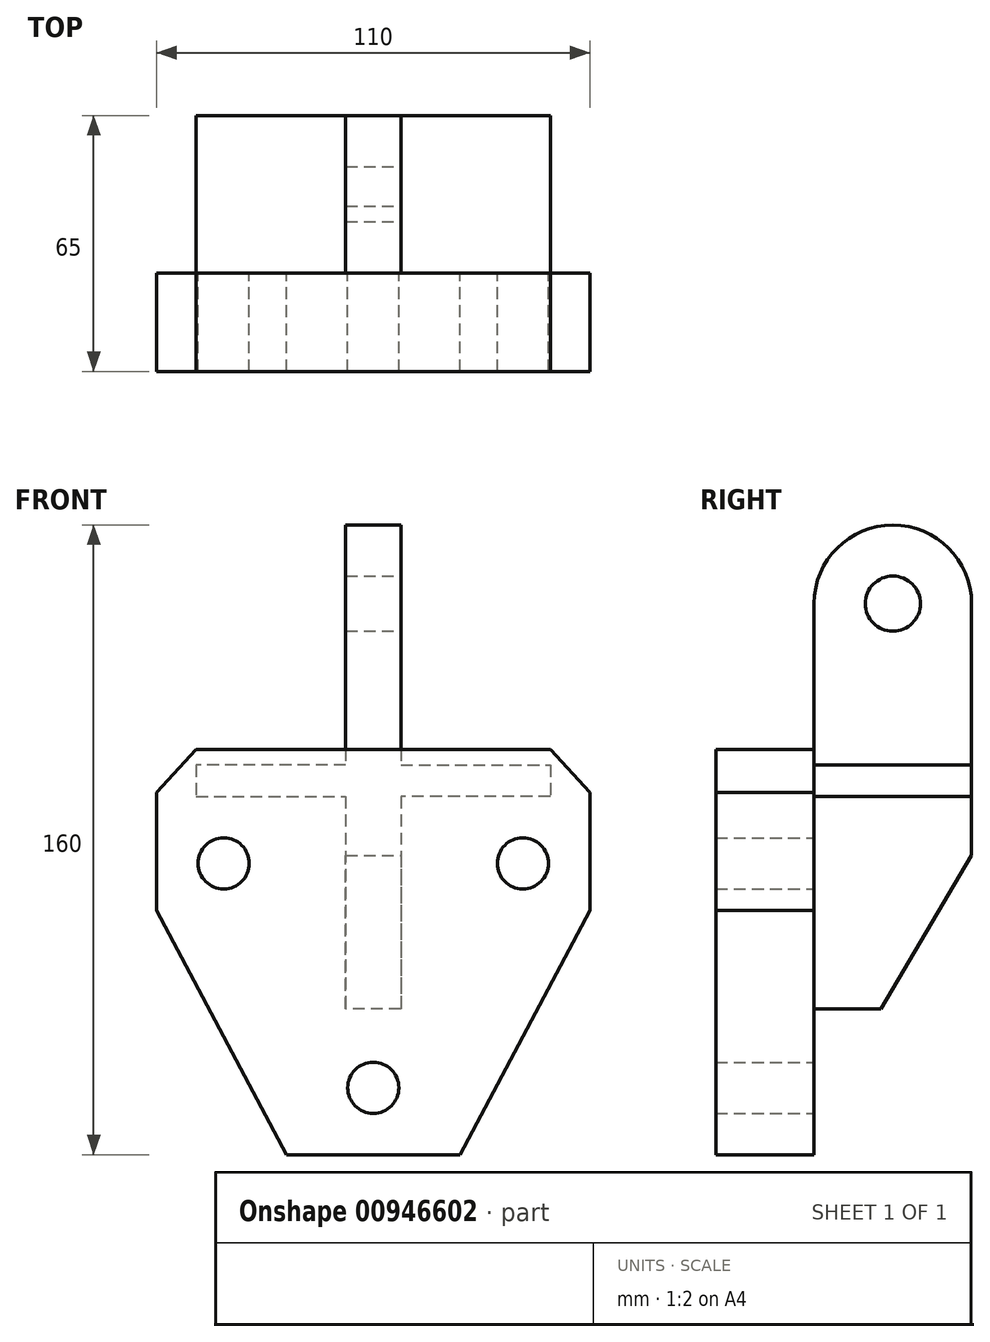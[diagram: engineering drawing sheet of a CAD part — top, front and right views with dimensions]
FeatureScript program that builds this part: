
annotation { "Feature Type Name" : "Feature", "Feature Type Description" : "" }
export const myFeature = defineFeature(function(context is Context, id is Id, definition is map)
    precondition{}
    {
        {
            var Q0;
            Q0=qCreatedBy(makeId("Front.planeOp"),FACE);
            var sketch = newSketch(context, id + "F0", { "sketchPlane" : qUnion([Q0])});
            skLineSegment(sketch, "E0", {"start": v(0, 51.49) * mm, "end": v(-45, 51.49) * mm});
            skLineSegment(sketch, "E1", {"start": v(-45, 51.49) * mm, "end": v(-55, 40.49) * mm});
            skLineSegment(sketch, "E2", {"start": v(-55, 40.49) * mm, "end": v(-55, 10.49) * mm});
            skLineSegment(sketch, "E3", {"start": v(-55, 10.49) * mm, "end": v(-22, -51.51) * mm});
            skLineSegment(sketch, "E4", {"start": v(-22, -51.51) * mm, "end": v(0, -51.51) * mm});
            skLineSegment(sketch, "E5", {"start": v(0, -51.51) * mm, "end": v(0, 51.49) * mm});
            skCircle(sketch, "E6", {"center": v(-38, 22.49) * mm, "radius": 6.5 * mm});
            skArc(sketch, "E7", {"start": v(0, -28.01) * mm, "mid": v(-6.5, -34.51) * mm, "end": v(0, -41.01) * mm});
            skLineSegment(sketch, "E8.MirrorCS", {"start": v(0, 51.49) * mm, "end": v(45, 51.49) * mm});
            skLineSegment(sketch, "E9.MirrorCS", {"start": v(45, 51.49) * mm, "end": v(55, 40.49) * mm});
            skLineSegment(sketch, "E10.MirrorCS", {"start": v(55, 40.49) * mm, "end": v(55, 10.49) * mm});
            skLineSegment(sketch, "E11.MirrorCS", {"start": v(55, 10.49) * mm, "end": v(22, -51.51) * mm});
            skLineSegment(sketch, "E12.MirrorCS", {"start": v(22, -51.51) * mm, "end": v(0, -51.51) * mm});
            skArc(sketch, "E13.MirrorCS", {"start": v(0, -28.01) * mm, "mid": v(6.5, -34.51) * mm, "end": v(0, -41.01) * mm});
            skCircle(sketch, "E14.MirrorC", {"center": v(38, 22.49) * mm, "radius": 6.5 * mm});
            skSolve(sketch);
        }
        {
            var Q0;
            Q0 = qSketchRegion(id + "F0", true);
            extrude(context, id + "F1", {"entities" : qUnion([Q0]), "depth" : 25 * mm, "offsetDistance" : 25 * mm});
        }
        {
            var Q0;
            Q0=makeQuery(id+"F1.opExtrude","CAP_FACE",FACE,{"disambiguationData":[OSD([sQuery(id+"F0.wireOp",EDGE,"E0"),sQuery(id+"F0.wireOp",EDGE,"E1"),sQuery(id+"F0.wireOp",EDGE,"E2"),sQuery(id+"F0.wireOp",EDGE,"E3"),sQuery(id+"F0.wireOp",EDGE,"E4"),sQuery(id+"F0.wireOp",EDGE,"E6"),sQuery(id+"F0.wireOp",EDGE,"E7"),sQuery(id+"F0.wireOp",EDGE,"E8.MirrorCS"),sQuery(id+"F0.wireOp",EDGE,"E9.MirrorCS"),sQuery(id+"F0.wireOp",EDGE,"E10.MirrorCS"),sQuery(id+"F0.wireOp",EDGE,"E11.MirrorCS"),sQuery(id+"F0.wireOp",EDGE,"E12.MirrorCS"),sQuery(id+"F0.wireOp",EDGE,"E13.MirrorCS"),sQuery(id+"F0.wireOp",EDGE,"E14.MirrorC")])],"isStart":true});
            var sketch = newSketch(context, id + "F2", { "sketchPlane" : qUnion([Q0])});
            skLineSegment(sketch, "E15", {"start": v(0, 108.49) * mm, "end": v(-7, 108.49) * mm});
            skLineSegment(sketch, "E16", {"start": v(-7, 108.49) * mm, "end": v(-7, 47.49) * mm});
            skLineSegment(sketch, "E17", {"start": v(-7, 47.49) * mm, "end": v(-45, 47.49) * mm});
            skLineSegment(sketch, "E18", {"start": v(-45, 47.49) * mm, "end": v(-45, 39.49) * mm});
            skLineSegment(sketch, "E19", {"start": v(-45, 39.49) * mm, "end": v(-7, 39.49) * mm});
            skLineSegment(sketch, "E20", {"start": v(-7, 39.49) * mm, "end": v(-7, -14.51) * mm});
            skLineSegment(sketch, "E21", {"start": v(-7, -14.51) * mm, "end": v(0, -14.51) * mm});
            skLineSegment(sketch, "E22.MirrorCS", {"start": v(0, 108.49) * mm, "end": v(7, 108.49) * mm});
            skLineSegment(sketch, "E23.MirrorCS", {"start": v(7, 108.49) * mm, "end": v(7, 47.49) * mm});
            skLineSegment(sketch, "E24.MirrorCS", {"start": v(7, 47.49) * mm, "end": v(45, 47.49) * mm});
            skLineSegment(sketch, "E25.MirrorCS", {"start": v(45, 47.49) * mm, "end": v(45, 39.49) * mm});
            skLineSegment(sketch, "E26.MirrorCS", {"start": v(45, 39.49) * mm, "end": v(7, 39.49) * mm});
            skLineSegment(sketch, "E27.MirrorCS", {"start": v(7, 39.49) * mm, "end": v(7, -14.51) * mm});
            skLineSegment(sketch, "E28.MirrorCS", {"start": v(7, -14.51) * mm, "end": v(0, -14.51) * mm});
            skSolve(sketch);
        }
        {
            var Q0;
            Q0 = qSketchRegion(id + "F2", true);
            extrude(context, id + "F3", {"entities" : qUnion([Q0]), "operationType" : NewBodyOperationType.ADD, "depth" : 40 * mm, "offsetDistance" : 25 * mm});
        }
        {
            var Q0;
            Q0=makeQuery(id+"F3.opExtrude","CAP_EDGE",EDGE,{"disambiguationData":[OSD([sQuery(id+"F2.wireOp",EDGE,"E15"),sQuery(id+"F2.wireOp",EDGE,"E22.MirrorCS")])],"isStart":true});
            var Q1;
            Q1=makeQuery(id+"F3.opExtrude","CAP_EDGE",EDGE,{"disambiguationData":[OSD([sQuery(id+"F2.wireOp",EDGE,"E15"),sQuery(id+"F2.wireOp",EDGE,"E22.MirrorCS")])],"isStart":false});
            fillet(context, id + "F4", {"entities" : qUnion([Q0, Q1]), "radius" : 20 * mm, "tangentPropagation" : true, "allowEdgeOverflow" : false});
        }
        {
            var Q0;
            Q0=makeQuery(id+"F3.opExtrude","SWEPT_FACE",FACE,{"disambiguationData":[OSD([sQuery(id+"F2.wireOp",EDGE,"E16")])]});
            var sketch = newSketch(context, id + "F5", { "sketchPlane" : qUnion([Q0])});
            skCircle(sketch, "E29", {"center": v(20, 88.49) * mm, "radius": 7 * mm});
            skLineSegment(sketch, "E30", {"start": v(40, 24.49) * mm, "end": v(17, -14.51) * mm});
            skLineSegment(sketch, "E31", {"start": v(17, -14.51) * mm, "end": v(40, -14.51) * mm});
            skLineSegment(sketch, "E32", {"start": v(40, -14.51) * mm, "end": v(40, 24.49) * mm});
            skSolve(sketch);
        }
        {
            var Q0;
            Q0 = qSketchRegion(id + "F5", true);
            extrude(context, id + "F6", {"entities" : qUnion([Q0]), "operationType" : NewBodyOperationType.REMOVE, "oppositeDirection" : true, "depth" : 25 * mm, "offsetDistance" : 25 * mm});
        }
    });
